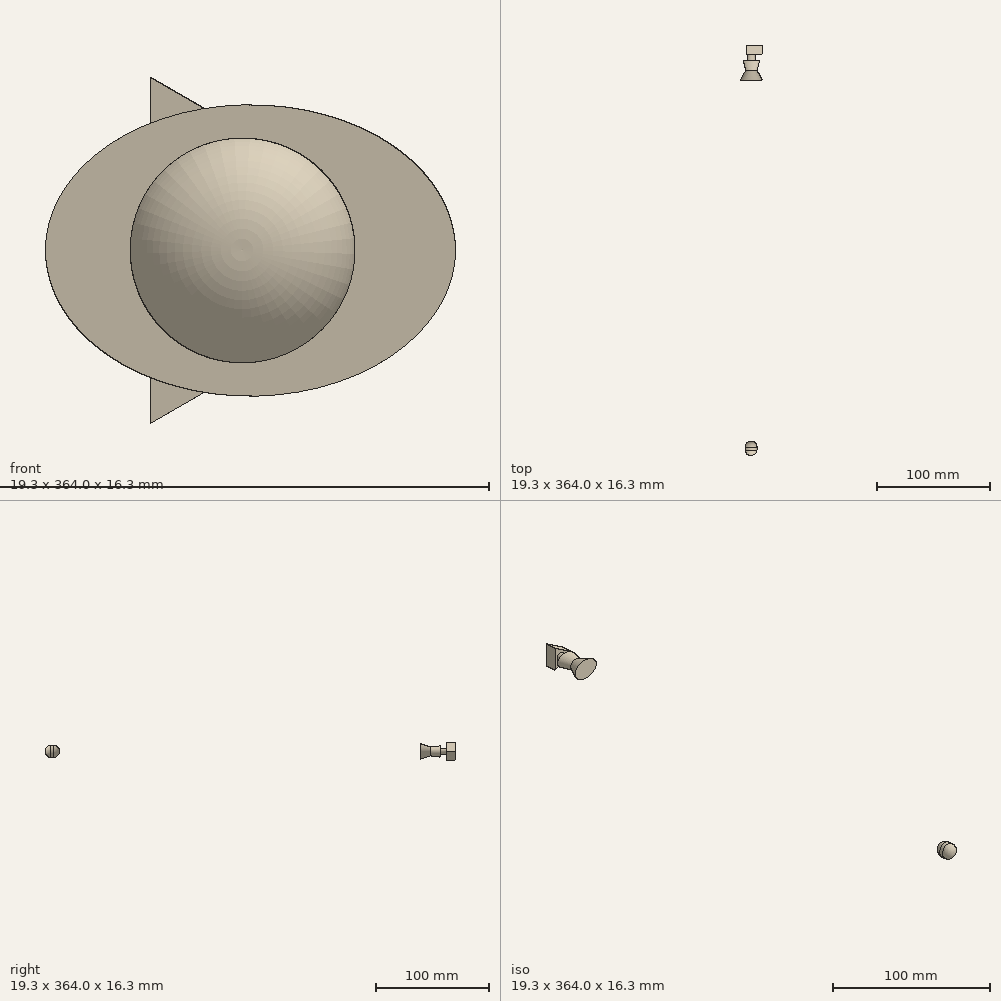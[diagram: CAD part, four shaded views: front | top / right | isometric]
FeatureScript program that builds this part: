
annotation { "Feature Type Name" : "Feature", "Feature Type Description" : "" }
export const myFeature = defineFeature(function(context is Context, id is Id, definition is map)
    precondition{}
    {
        {
            var Q0;
            Q0=qCreatedBy(makeId("Front.planeOp"),FACE);
            var sketch = newSketch(context, id + "F0", { "sketchPlane" : qUnion([Q0])});
            skLineSegment(sketch, "E0", {"start": v(0, 0) * mm, "end": v(0, 16.3) * mm});
            skLineSegment(sketch, "E1", {"start": v(0, 16.3) * mm, "end": v(14.12, 8.15) * mm});
            skLineSegment(sketch, "E2", {"start": v(14.12, 8.15) * mm, "end": v(0, 0) * mm});
            skSolve(sketch);
        }
        {
            var Q0;
            Q0=makeQuery(id+"F0.imprint","IMPRINT",FACE,{"disambiguationData":[TD([[makeQuery(id+"F0.imprint","IMPRINT",EDGE,{"derivedFrom":sQuery(id+"F0.wireOp",EDGE,"E0")}),-1.0]])]});
            extrude(context, id + "F1", {"entities" : qUnion([Q0]), "depth" : 8.13 * mm});
        }
        {
            var Q0;
            Q0=makeQuery(id+"F1.opExtrude","CAP_FACE",FACE,{"disambiguationData":[OSD([sQuery(id+"F0.wireOp",EDGE,"E0"),sQuery(id+"F0.wireOp",EDGE,"E1"),sQuery(id+"F0.wireOp",EDGE,"E2")])],"isStart":false});
            var sketch = newSketch(context, id + "F2", { "sketchPlane" : qUnion([Q0])});
            skEllipse(sketch, "E3", {"center": v(4.7, 8.15) * mm, "majorRadius": 3.18 * mm, "minorRadius": 2.67 * mm, "majorAxis": v(1, 0)});
            skSolve(sketch);
        }
        {
            var Q0;
            Q0=makeQuery(id+"F2.imprint","IMPRINT",FACE,{"disambiguationData":[TD([[makeQuery(id+"F2.imprint","IMPRINT",EDGE,{"derivedFrom":makeQuery(id+"F1.opExtrude","CAP_EDGE",EDGE,{"disambiguationData":[OSD([sQuery(id+"F0.wireOp",EDGE,"E0")])],"isStart":false})}),-1.0]])]});
            cPlane(context, id + "F3", {"entities" : qUnion([Q0]), "cplaneType" : CPlaneType.OFFSET, "offset" : 4.83 * mm, "width" : 152.4 * mm, "height" : 152.4 * mm});
        }
        {
            var Q0;
            Q0=qCreatedBy(id+"F3.planeOp",FACE);
            var sketch = newSketch(context, id + "F4", { "sketchPlane" : qUnion([Q0])});
            skEllipse(sketch, "E4", {"center": v(4.7, 8.15) * mm, "majorRadius": 3.56 * mm, "minorRadius": 2.8 * mm, "majorAxis": v(1, 0)});
            skSolve(sketch);
        }
        {
            var Q1;
            Q1=makeQuery(id+"F2.imprint","IMPRINT",FACE,{"disambiguationData":[TD([[makeQuery(id+"F2.imprint","IMPRINT",EDGE,{"derivedFrom":sQuery(id+"F2.wireOp",EDGE,"E3")}),1.0]])]});
            var Q2;
            Q2=makeQuery(id+"F4.imprint","IMPRINT",FACE,{"disambiguationData":[TD([[makeQuery(id+"F4.imprint","IMPRINT",EDGE,{"derivedFrom":sQuery(id+"F4.wireOp",EDGE,"E4")}),1.0]])]});
            loft(context, id + "F5", {"operationType" : NewBodyOperationType.ADD, "sheetProfilesArray" : [{ "sheetProfileEntities" : qUnion([Q1]) }, { "sheetProfileEntities" : qUnion([Q2]) }]});
        }
        {
            var Q0;
            Q0=makeQuery(id+"F5.opLoft","CAP_FACE",FACE,{"disambiguationData":[OSD([makeQuery(id+"F4.imprint","IMPRINT",FACE,{"disambiguationData":[TD([[makeQuery(id+"F4.imprint","IMPRINT",EDGE,{"derivedFrom":sQuery(id+"F4.wireOp",EDGE,"E4")}),1.0]])]})])],"isStart":true});
            var sketch = newSketch(context, id + "F6", { "sketchPlane" : qUnion([Q0])});
            skEllipse(sketch, "E5", {"center": v(4.7, 8.15) * mm, "majorRadius": 7.62 * mm, "minorRadius": 5.08 * mm, "majorAxis": v(1, 0)});
            skSolve(sketch);
        }
        {
            var Q0;
            Q0=qCreatedBy(id+"F3.planeOp",FACE);
            cPlane(context, id + "F7", {"entities" : qUnion([Q0]), "cplaneType" : CPlaneType.OFFSET, "offset" : 9.14 * mm, "width" : 152.4 * mm, "height" : 152.4 * mm});
        }
        {
            var Q0;
            Q0=qCreatedBy(id+"F7.planeOp",FACE);
            var sketch = newSketch(context, id + "F8", { "sketchPlane" : qUnion([Q0])});
            skEllipse(sketch, "E6", {"center": v(4.7, 8.15) * mm, "majorRadius": 4.95 * mm, "minorRadius": 3.94 * mm, "majorAxis": v(1, 0)});
            skLineSegment(sketch, "E7", {"start": v(-0.24, 8.15) * mm, "end": v(9.66, 8.15) * mm});
            skSolve(sketch);
        }
        {
            var Q1;
            Q1 = qSketchRegion(id + "F6", true);
            var Q2;
            Q2 = qSketchRegion(id + "F8", true);
            loft(context, id + "F9", {"operationType" : NewBodyOperationType.ADD, "sheetProfilesArray" : [{ "sheetProfileEntities" : qUnion([Q1]) }, { "sheetProfileEntities" : qUnion([Q2]) }]});
        }
        {
            var Q0;
            Q0=qCreatedBy(id+"F7.planeOp",FACE);
            cPlane(context, id + "F10", {"entities" : qUnion([Q0]), "cplaneType" : CPlaneType.OFFSET, "offset" : 8.64 * mm, "width" : 152.4 * mm, "height" : 152.4 * mm});
        }
        {
            var Q0;
            Q0=qCreatedBy(id+"F10.planeOp",FACE);
            var sketch = newSketch(context, id + "F11", { "sketchPlane" : qUnion([Q0])});
            skEllipse(sketch, "E8", {"center": v(4.7, 8.15) * mm, "majorRadius": 9.65 * mm, "minorRadius": 6.86 * mm, "majorAxis": v(-1, 0)});
            skSolve(sketch);
        }
        {
            var Q0;
            Q0 = qSketchRegion(id + "F8", true);
            var Q1;
            Q1 = qSketchRegion(id + "F11", true);
            loft(context, id + "F12", {"sheetProfilesArray" : [{ "sheetProfileEntities" : qUnion([Q0]) }, { "sheetProfileEntities" : qUnion([Q1]) }]});
        }
        {
            var Q0;
            Q0=makeQuery(id+"F1.opExtrude","CAP_VERTEX",VERTEX,{"disambiguationData":[OSD([sQuery(id+"F0.wireOp",EDGE,"E1"),sQuery(id+"F0.wireOp",EDGE,"E2")])],"isStart":false});
            var Q1;
            Q1=qCreatedBy(makeId("Top.planeOp"),FACE);
            cPlane(context, id + "F13", {"entities" : qUnion([Q0, Q1]), "cplaneType" : CPlaneType.PLANE_POINT, "offset" : 25.4 * mm, "width" : 152.4 * mm, "height" : 152.4 * mm});
        }
        {
            var Q0;
            Q0=qCreatedBy(id+"F13.planeOp",FACE);
            var sketch = newSketch(context, id + "F14", { "sketchPlane" : qUnion([Q0])});
            skLineSegment(sketch, "E9", {"start": v(-7.49, 0) * mm, "end": v(-13.65, -31.74) * mm});
            skLineSegment(sketch, "E10", {"start": v(-13.65, -31.74) * mm, "end": v(22.32, -31.74) * mm});
            skLineSegment(sketch, "E11", {"start": v(22.32, -31.74) * mm, "end": v(16.16, 0) * mm});
            skArc(sketch, "E12", {"start": v(-13.65, -31.74) * mm, "mid": v(4.34, -351.85) * mm, "end": v(22.32, -31.74) * mm});
            skLineSegment(sketch, "E13", {"start": v(-7.49, 0) * mm, "end": v(16.16, 0) * mm});
            skSolve(sketch);
        }
        {
            var Q0;
            Q0 = qSketchRegion(id + "F14", true);
            var Q1;
            Q1=sQuery(id+"F14.wireOp",EDGE,"E13");
            revolve(context, id + "F15", {"operationType" : NewBodyOperationType.INTERSECT, "entities" : qUnion([Q0]), "axis" : qUnion([Q1]), "revolveType" : RevolveType.FULL});
        }
        {
            var Q0;
            Q0=qCreatedBy(id+"F13.planeOp",FACE);
            var sketch = newSketch(context, id + "F16", { "sketchPlane" : qUnion([Q0])});
            skLineSegment(sketch, "E14", {"start": v(4.34, -363.98) * mm, "end": v(4.34, -351.28) * mm});
            skLineSegment(sketch, "E15", {"start": v(-0.96, -356.6) * mm, "end": v(-0.96, -359.13) * mm});
            skArc(sketch, "E16", {"start": v(4.34, -351.28) * mm, "mid": v(0.6, -352.85) * mm, "end": v(-0.96, -356.6) * mm});
            skArc(sketch, "E17", {"start": v(-0.96, -359.13) * mm, "mid": v(0.62, -362.71) * mm, "end": v(4.34, -363.98) * mm});
            skSolve(sketch);
        }
        {
            var Q0;
            Q0=makeQuery(id+"F16.imprint","IMPRINT",FACE,{"disambiguationData":[TD([[makeQuery(id+"F16.imprint","IMPRINT",EDGE,{"derivedFrom":sQuery(id+"F16.wireOp",EDGE,"E14")}),1.0]])]});
            var Q1;
            Q1=sQuery(id+"F16.wireOp",EDGE,"E14");
            revolve(context, id + "F17", {"operationType" : NewBodyOperationType.ADD, "entities" : qUnion([Q0]), "axis" : qUnion([Q1]), "revolveType" : RevolveType.FULL});
        }
    });
